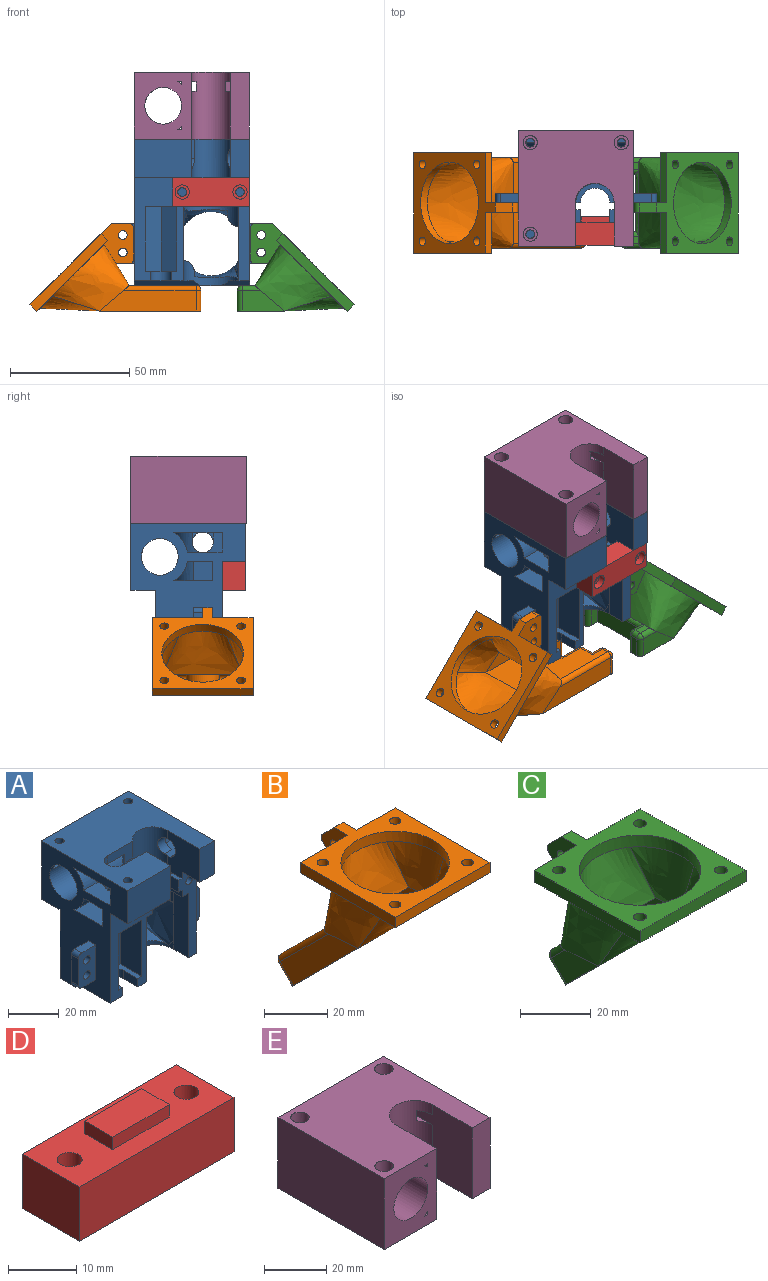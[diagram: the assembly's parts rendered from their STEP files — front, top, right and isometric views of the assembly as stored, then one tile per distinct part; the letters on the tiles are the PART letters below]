
ASSEMBLY  parts=5 mates=4
PART A: 179 faces, bbox 68x48.6x61.8 mm
  f0: plane 61.5x48.25mm, normal (1,0,0), area 1645.7mm2, adj f1,f4,f22,f24,f35,f36,f37,f43
  f1: plane 48.4x8.88mm, normal (0,0,-1), area 407.8mm2, adj f0,f5,f43,f44,f86,f87,f90,f100
  f2: plane 43.38x26.08mm, normal (0,-1,0), area 533.4mm2, adj f6,f8,f9,f13,f25,f44,f45,f47
  f3: cylinder r=4.38mm len=8.75mm, axis (0,0,-1), area 55mm2, adj f8,f9,f172,f175
  f4: plane 43.38x10.08mm, normal (0,-1,0), area 239.6mm2, adj f0,f7,f12,f29,f45,f53,f120,f164
  f5: cylinder r=11.7mm len=23.4mm, axis (0,0,1), area 147.8mm2, adj f1,f6,f7,f11,f39,f41,f174,f175
  f6: plane 31.25x8.13mm, normal (1,0,0), area 253.9mm2, adj f2,f5,f38,f40,f45,f175
  f7: plane 31.25x8.13mm, normal (-1,0,0), area 253.9mm2, adj f4,f5,f40,f41,f45,f176
  f8: plane 8.13x4mm, normal (-1,0,0), area 32.5mm2, adj f2,f3,f172,f175
  f9: plane 8.13x4mm, normal (1,0,0), area 32.5mm2, adj f2,f3,f172,f175
  f10: plane 8.56x1.84mm, normal (-1,0,0), area 8mm2, adj f40,f42,f173
  f11: plane 8.56x1.84mm, normal (1,0,0), area 8mm2, adj f5,f39,f174
  f12: plane 8.13x3.25mm, normal (-1,0,0), area 25.8mm2, adj f4,f45,f59,f109,f116,f166
  f13: plane 8.13x3.25mm, normal (1,0,0), area 25.8mm2, adj f2,f31,f45,f59,f119,f162
  f14: plane 6.57x2.69mm, normal (0,0,1), area 13.5mm2, adj f146,f147,f148,f160
  f15: plane 2.46x1.42mm, normal (0,0,-1), area 1.7mm2, adj f142,f144,f160
  f16: plane 2.46x1.42mm, normal (0,0,-1), area 1.7mm2, adj f143,f145,f160
  f17: plane 3.62x3.46mm, normal (0,1,0), area 12.6mm2, adj f141,f144,f145,f160
  f18: plane 6.57x2.69mm, normal (0,0,1), area 13.5mm2, adj f155,f156,f157,f160
  f19: plane 2.46x1.42mm, normal (0,0,-1), area 1.7mm2, adj f151,f153,f160
  f20: plane 2.46x1.42mm, normal (0,0,-1), area 1.7mm2, adj f152,f154,f160
  f21: plane 3.62x3.46mm, normal (0,1,0), area 12.6mm2, adj f150,f153,f154,f160
  f22: plane 48.4x48.25mm, normal (0,0,1), area 1761.2mm2, adj f0,f25,f26,f28,f29,f44,f46,f51
  f23: plane 8.13x6.5mm, normal (-1,0,0), area 33.5mm2, adj f24,f48,f127,f129,f130
  f24: plane 48.4x26.26mm, normal (0,0,-1), area 481.3mm2, adj f0,f23,f26,f28,f29,f44,f54,f56
  f25: plane 19.25x18.13mm, normal (1,0,0), area 267.5mm2, adj f2,f22,f28,f46,f47,f48,f111,f119
  f26: cylinder r=4.38mm len=8.75mm, axis (0,0,-1), area 55mm2, adj f22,f24,f128,f129
  f27: cylinder r=4.38mm len=5.17mm, axis (-1,0,0), area 22.2mm2, adj f28,f48,f58,f128
  f28: cylinder r=8.12mm len=19.25mm, axis (0,0,-1), area 408.2mm2, adj f22,f24,f25,f27,f29,f48,f55,f62
  f29: plane 19.25x18.13mm, normal (-1,0,0), area 288.1mm2, adj f4,f22,f24,f28,f32,f52,f53,f55
  f30: plane 8.13x3.34mm, normal (0,1,0), area 27.2mm2, adj f34,f36,f107,f124
  f31: plane 5.73x5.13mm, normal (0,0,1), area 24.6mm2, adj f13,f65,f113,f118,f119,f123
  f32: plane 5.73x5.13mm, normal (0,0,-1), area 24.6mm2, adj f29,f64,f108,f114,f116,f121
  f33: cylinder r=12.12mm len=22.89mm, axis (0,0,1), area 89.5mm2, adj f34,f35,f36,f57,f105,f106
  f34: plane 21.95x10.6mm, normal (0,0,-1), area 123mm2, adj f30,f33,f44,f49,f57,f106,f107,f124
  f35: plane 5.95x2.47mm, normal (0,0,-1), area 13.1mm2, adj f0,f33,f57,f105
  f36: plane 48.4x16.26mm, normal (0,0,1), area 328.5mm2, adj f0,f30,f33,f44,f49,f57,f105,f106
  f37: plane 5.93x5.13mm, normal (0,0,-1), area 25.2mm2, adj f0,f91,f94,f96,f97,f102
  f38: bspline ~31.25x19.88mm, area 392.3mm2, adj f6,f40,f42,f43,f85,f174
  f39: bspline ~23.4x19.88mm, area 177.2mm2, adj f5,f11,f41,f43,f174
  f40: cylinder r=11.7mm len=23.4mm, axis (0,0,1), area 123.4mm2, adj f6,f7,f10,f38,f42,f45,f173
  f41: bspline ~31.25x19.88mm, area 392.3mm2, adj f5,f7,f39,f43,f84,f173
  f42: bspline ~23.4x19.88mm, area 177.2mm2, adj f10,f38,f40,f43,f173
  f43: plane 48.4x33.25mm, normal (0,1,0), area 1029mm2, adj f0,f1,f38,f39,f41,f42,f44,f50
  f44: plane 61.5x48.25mm, normal (-1,0,0), area 1646.4mm2, adj f1,f2,f22,f24,f34,f36,f43,f46
  f45: plane 23.4x19.83mm, normal (0,0,-1), area 169.4mm2, adj f2,f4,f6,f7,f12,f13,f40,f59
  f46: plane 24.08x16.13mm, normal (0,-1,0), area 388.2mm2, adj f22,f25,f44,f47
  f47: plane 24.08x10mm, normal (0,0,-1), area 240.8mm2, adj f2,f25,f44,f46
  f48: plane 24.24x22.6mm, normal (0,0,1), area 300.1mm2, adj f23,f25,f27,f28,f44,f54,f58,f124
  f49: plane 9.74x8.13mm, normal (0,1,0), area 79.2mm2, adj f34,f36,f44,f124
  f50: plane 48.4x10.25mm, normal (0,0,-1), area 496.1mm2, adj f0,f43,f44,f51
  f51: plane 48.4x28.25mm, normal (0,1,0), area 1367.3mm2, adj f0,f22,f44,f50
  f52: plane 16.13x8.08mm, normal (0,-1,0), area 130.2mm2, adj f0,f22,f29,f53
  f53: plane 10x8.08mm, normal (0,0,-1), area 80.7mm2, adj f0,f4,f29,f52
  f54: cylinder r=11.7mm len=48.4mm, axis (-1,0,0), area 332.2mm2, adj f0,f24,f44,f48,f55,f58
  f55: plane 20.6x8.24mm, normal (0,0,1), area 100.9mm2, adj f0,f28,f29,f54,f56,f58,f63,f125
  f56: plane 8.13x4.08mm, normal (0,1,0), area 33.1mm2, adj f0,f24,f55,f63
  f57: cylinder r=11.7mm len=48.4mm, axis (-1,0,0), area 332.2mm2, adj f0,f33,f34,f35,f36,f44
  f58: cylinder r=12.12mm len=24.03mm, axis (0,0,1), area 95.3mm2, adj f24,f27,f48,f54,f55,f126,f128
  f59: cylinder r=8.12mm len=16.25mm, axis (0,0,-1), area 83mm2, adj f12,f13,f45,f60,f64,f65
  f60: plane 16.25x8.13mm, normal (0,0,-1), area 44.8mm2, adj f59,f61,f64,f65
  f61: cylinder r=6.12mm len=12.25mm, axis (0,0,-1), area 110.6mm2, adj f60,f62,f64,f65
  f62: plane 16.25x8.13mm, normal (0,0,1), area 44.8mm2, adj f28,f61,f64,f65
  f63: plane 12.5x8.13mm, normal (1,0,0), area 85.4mm2, adj f24,f55,f56,f125
  f64: plane 9.46x6mm, normal (0,-1,0), area 51.1mm2, adj f28,f32,f59,f60,f61,f62,f108,f109
  f65: plane 9.46x6mm, normal (0,-1,0), area 51.1mm2, adj f28,f31,f59,f60,f61,f62,f111,f112
  f66: plane 7.65x4mm, normal (0,0,-1), area 30.6mm2, adj f0,f67,f69,f79
  f67: plane 16.95x9.65mm, normal (0,1,0), area 140.9mm2, adj f0,f66,f68,f70,f78,f79,f82,f83
  f68: plane 7.65x4mm, normal (0,0,1), area 30.6mm2, adj f0,f67,f69,f78
  f69: plane 16.95x9.65mm, normal (0,-1,0), area 140.9mm2, adj f0,f66,f68,f70,f78,f79,f82,f83
  f70: plane 12.95x4mm, normal (1,0,0), area 51.8mm2, adj f67,f69,f78,f79
  f71: plane 7.65x4mm, normal (0,0,-1), area 30.6mm2, adj f44,f72,f74,f76
  f72: plane 16.95x9.65mm, normal (0,-1,0), area 140.9mm2, adj f44,f71,f73,f75,f76,f77,f80,f81
  f73: plane 7.65x4mm, normal (0,0,1), area 30.6mm2, adj f44,f72,f74,f77
  f74: plane 16.95x9.65mm, normal (0,1,0), area 140.9mm2, adj f44,f71,f73,f75,f76,f77,f80,f81
  f75: plane 12.95x4mm, normal (-1,0,0), area 51.8mm2, adj f72,f74,f76,f77
  f76: cylinder r=2mm len=4mm, axis (0,1,0), area 12.6mm2, adj f71,f72,f74,f75
  f77: cylinder r=2mm len=4mm, axis (0,-1,0), area 12.6mm2, adj f72,f73,f74,f75
  f78: cylinder r=2mm len=4mm, axis (0,1,0), area 12.6mm2, adj f67,f68,f69,f70
  f79: cylinder r=2mm len=4mm, axis (0,-1,0), area 12.6mm2, adj f66,f67,f69,f70
  f80: cylinder r=1.82mm len=4mm, axis (0,1,0), area 45.9mm2, adj f72,f74
  f81: cylinder r=1.82mm len=4mm, axis (0,1,0), area 45.9mm2, adj f72,f74
  f82: cylinder r=1.82mm len=4mm, axis (0,1,0), area 45.9mm2, adj f67,f69
  f83: cylinder r=1.82mm len=4mm, axis (0,1,0), area 45.9mm2, adj f67,f69
  f84: plane 1.91x0.01mm, normal (0,0,-1), area 0mm2, adj f41,f173
  f85: plane 1.91x0.01mm, normal (0,0,1), area 0mm2, adj f38,f174
  f86: plane 7.36x5.13mm, normal (-1,0,0), area 29.4mm2, adj f1,f89,f90,f98,f100,f104
  f87: plane 7.36x5.13mm, normal (1,0,0), area 29.4mm2, adj f1,f88,f90,f99,f100,f104
  f88: plane 5.13x3mm, normal (0.5,0,-0.87), area 17.8mm2, adj f87,f89,f90,f104
  f89: plane 5.13x3mm, normal (-0.5,0,-0.87), area 17.8mm2, adj f86,f88,f90,f104
  f90: plane 9.09x6mm, normal (0,1,0), area 49.3mm2, adj f1,f86,f87,f88,f89
  f91: plane 5.13x3mm, normal (0.87,0,-0.5), area 17.8mm2, adj f37,f93,f94,f102
  f92: plane 5.93x5.13mm, normal (0,0,1), area 25.2mm2, adj f0,f93,f94,f95,f97,f102
  f93: plane 5.13x3mm, normal (0.87,0,0.5), area 17.8mm2, adj f91,f92,f94,f102
  f94: plane 7.66x6mm, normal (0,1,0), area 40.8mm2, adj f0,f37,f91,f92,f93
  f95: plane 3x2.13mm, normal (-0.87,0,0.5), area 7.4mm2, adj f92,f96,f97,f102
  f96: plane 3x2.13mm, normal (-0.87,0,-0.5), area 7.4mm2, adj f37,f95,f97,f102
  f97: plane 6x2.47mm, normal (0,-1,0), area 9.6mm2, adj f0,f37,f92,f95,f96
  f98: plane 3x2.13mm, normal (-0.5,0,0.87), area 7.4mm2, adj f86,f99,f100,f104
  f99: plane 3x2.13mm, normal (0.5,0,0.87), area 7.4mm2, adj f87,f98,f100,f104
  f100: plane 6x3.89mm, normal (0,-1,0), area 18.2mm2, adj f1,f86,f87,f98,f99
  f101: cylinder r=1.82mm len=3.65mm, axis (0,1,0), area 34.4mm2, adj f43,f102
  f102: plane 6.93x6mm, normal (0,-1,0), area 20.7mm2, adj f37,f91,f92,f93,f95,f96,f101
  f103: cylinder r=1.82mm len=3.65mm, axis (0,1,0), area 34.4mm2, adj f43,f104
  f104: plane 6.93x6mm, normal (0,-1,0), area 20.7mm2, adj f86,f87,f88,f89,f98,f99,f103
  f105: plane 8.13x4.75mm, normal (0,1,0), area 38.6mm2, adj f0,f33,f35,f36
  f106: plane 8.13x4.75mm, normal (0,1,0), area 38.6mm2, adj f33,f34,f36,f107
  f107: plane 8.13x8.13mm, normal (-1,0,0), area 66mm2, adj f30,f34,f36,f106
  f108: plane 5.13x3mm, normal (-0.87,0,-0.5), area 17.8mm2, adj f32,f64,f110,f121
  f109: plane 5.73x5.13mm, normal (0,0,1), area 24.6mm2, adj f12,f64,f110,f115,f116,f121
  f110: plane 5.13x3mm, normal (-0.87,0,0.5), area 17.8mm2, adj f64,f108,f109,f121
  f111: plane 5.73x5.13mm, normal (0,0,-1), area 24.6mm2, adj f25,f65,f112,f117,f119,f123
  f112: plane 5.13x3mm, normal (0.87,0,-0.5), area 17.8mm2, adj f65,f111,f113,f123
  f113: plane 5.13x3mm, normal (0.87,0,0.5), area 17.8mm2, adj f31,f65,f112,f123
  f114: plane 3x2.13mm, normal (0.87,0,-0.5), area 7.4mm2, adj f32,f115,f116,f121
  f115: plane 3x2.13mm, normal (0.87,0,0.5), area 7.4mm2, adj f109,f114,f116,f121
  f116: plane 6x4.27mm, normal (0,1,0), area 19.9mm2, adj f12,f29,f32,f109,f114,f115,f164,f165
  f117: plane 3x2.13mm, normal (-0.87,0,-0.5), area 7.4mm2, adj f111,f118,f119,f123
  f118: plane 3x2.13mm, normal (-0.87,0,0.5), area 7.4mm2, adj f31,f117,f119,f123
  f119: plane 6x4.27mm, normal (0,1,0), area 19.9mm2, adj f13,f25,f31,f111,f117,f118,f161,f162
  f120: cylinder r=1.82mm len=3.65mm, axis (0,-1,0), area 34.4mm2, adj f4,f121
  f121: plane 6.93x6mm, normal (0,1,0), area 20.7mm2, adj f32,f108,f109,f110,f114,f115,f120
  f122: cylinder r=1.82mm len=3.65mm, axis (0,-1,0), area 34.4mm2, adj f2,f123
  f123: plane 6.93x6mm, normal (0,1,0), area 20.7mm2, adj f31,f111,f112,f113,f117,f118,f122
  f124: cylinder r=4.38mm len=16.13mm, axis (0,0,-1), area 244.1mm2, adj f30,f34,f36,f48,f49,f167
  f125: cylinder r=4.38mm len=8.13mm, axis (-1,0,0), area 41.7mm2, adj f24,f29,f55,f63
  f126: cylinder r=4.38mm len=8.13mm, axis (-1,0,0), area 48.9mm2, adj f24,f28,f55,f58
  f127: cylinder r=4.38mm len=4.06mm, axis (-1,0,0), area 20.8mm2, adj f23,f25,f48,f129
  f128: plane 14.15x8.06mm, normal (0,-1,0), area 74.7mm2, adj f22,f24,f26,f27,f28,f58
  f129: plane 12.88x8.06mm, normal (0,1,0), area 67.8mm2, adj f22,f23,f24,f25,f26,f127
  f130: plane 20.08x8.13mm, normal (0,1,0), area 134.5mm2, adj f23,f24,f44,f48,f132,f133,f139
  f131: plane 8.13x3mm, normal (-0.87,0.5,0), area 28.1mm2, adj f48,f132,f135,f137,f159
  f132: plane 5x4.13mm, normal (-1,0,0), area 20.6mm2, adj f48,f130,f131,f139
  f133: plane 5x4.13mm, normal (1,0,0), area 20.6mm2, adj f48,f130,f134,f139
  f134: plane 8.13x3mm, normal (0.87,0.5,0), area 28.1mm2, adj f48,f133,f135,f138,f159
  f135: plane 8.13x3.46mm, normal (0,1,0), area 28.1mm2, adj f48,f131,f134,f159
  f136: plane 4x3.46mm, normal (0,-1,0), area 13.9mm2, adj f137,f138,f139,f159
  f137: plane 4x3mm, normal (-0.87,-0.5,0), area 13.9mm2, adj f131,f136,f139,f159
  f138: plane 4x3mm, normal (0.87,-0.5,0), area 13.9mm2, adj f134,f136,f139,f159
  f139: plane 6.93x5mm, normal (0,0,-1), area 19.1mm2, adj f130,f132,f133,f136,f137,f138
  f140: cylinder r=1.82mm len=4mm, axis (0,0,1), area 45.9mm2, adj f22,f141
  f141: plane 6.93x6mm, normal (0,0,-1), area 20.7mm2, adj f17,f140,f144,f145,f146,f147,f148
  f142: plane 3.21x2.46mm, normal (1,0,0), area 3.2mm2, adj f15,f148,f160
  f143: plane 3.21x2.46mm, normal (-1,0,0), area 3.2mm2, adj f16,f147,f160
  f144: plane 4x3mm, normal (0.87,0.5,0), area 13.7mm2, adj f15,f17,f141,f148,f160
  f145: plane 4x3mm, normal (-0.87,0.5,0), area 13.7mm2, adj f16,f17,f141,f147,f160
  f146: plane 8.13x3.46mm, normal (0,-1,0), area 28.1mm2, adj f14,f141,f147,f148
  f147: plane 8.14x3.02mm, normal (-0.87,-0.5,0), area 28mm2, adj f14,f141,f143,f145,f146,f160
  f148: plane 8.14x3.02mm, normal (0.87,-0.5,0), area 28mm2, adj f14,f141,f142,f144,f146,f160
  f149: cylinder r=1.82mm len=4mm, axis (0,0,1), area 45.9mm2, adj f22,f150
  f150: plane 6.93x6mm, normal (0,0,-1), area 20.7mm2, adj f21,f149,f153,f154,f155,f156,f157
  f151: plane 3.21x2.46mm, normal (1,0,0), area 3.2mm2, adj f19,f157,f160
  f152: plane 3.21x2.46mm, normal (-1,0,0), area 3.2mm2, adj f20,f156,f160
  f153: plane 4x3mm, normal (0.87,0.5,0), area 13.7mm2, adj f19,f21,f150,f157,f160
  f154: plane 4x3mm, normal (-0.87,0.5,0), area 13.7mm2, adj f20,f21,f150,f156,f160
  f155: plane 8.13x3.46mm, normal (0,-1,0), area 28.1mm2, adj f18,f150,f156,f157
  f156: plane 8.14x3.02mm, normal (-0.87,-0.5,0), area 28mm2, adj f18,f150,f152,f154,f155,f160
  f157: plane 8.14x3.02mm, normal (0.87,-0.5,0), area 28mm2, adj f18,f150,f151,f153,f155,f160
  f158: cylinder r=1.82mm len=4mm, axis (0,0,1), area 45.9mm2, adj f22,f159
  f159: plane 6.93x6mm, normal (0,0,-1), area 20.7mm2, adj f131,f134,f135,f136,f137,f138,f158
  f160: cylinder r=7.7mm len=48.4mm, axis (-1,0,0), area 2266.9mm2, adj f0,f14,f15,f16,f17,f18,f19,f20
  f161: plane 5.13x2mm, normal (0,0,1), area 10.3mm2, adj f2,f25,f119,f163
  f162: plane 5.13x2mm, normal (0,0,-1), area 10.3mm2, adj f2,f13,f119,f163
  f163: plane 5.75x5.13mm, normal (1,0,0), area 29.5mm2, adj f2,f119,f161,f162
  f164: plane 5.13x2mm, normal (0,0,1), area 10.3mm2, adj f4,f29,f116,f165
  f165: plane 5.75x5.13mm, normal (-1,0,0), area 29.5mm2, adj f4,f116,f164,f166
  f166: plane 5.13x2mm, normal (0,0,-1), area 10.3mm2, adj f4,f12,f116,f165
  f167: plane 15.86x13.4mm, normal (0,0,-1), area 126.5mm2, adj f2,f124,f168,f169,f170,f171
  f168: plane 27.25x11.99mm, normal (1,0,0), area 326.8mm2, adj f2,f167,f169,f172
  f169: plane 27.25x6.7mm, normal (0.5,-0.87,0), area 210.8mm2, adj f167,f168,f170,f172
  f170: plane 27.25x6.7mm, normal (-0.5,-0.87,0), area 210.8mm2, adj f167,f169,f171,f172
  f171: plane 27.25x11.99mm, normal (-1,0,0), area 326.8mm2, adj f2,f167,f170,f172
  f172: plane 15.86x13.4mm, normal (0,0,1), area 85.5mm2, adj f2,f3,f8,f9,f168,f169,f170,f171
  f173: cylinder r=5mm len=19.88mm, axis (0,1,0), area 96.3mm2, adj f10,f40,f41,f42,f43,f84
  f174: cylinder r=5mm len=19.88mm, axis (0,1,0), area 96.3mm2, adj f5,f11,f38,f39,f43,f85
  f175: plane 24.72x17.13mm, normal (0,0,-1), area 261.5mm2, adj f2,f3,f5,f6,f8,f9,f44,f177
  f176: plane 17.13x8.72mm, normal (0,0,-1), area 88.7mm2, adj f0,f4,f5,f7,f178
  f177: plane 28.52x2.3mm, normal (0,-0.71,-0.71), area 74.2mm2, adj f1,f5,f44,f175
  f178: plane 12.52x2.3mm, normal (0,-0.71,-0.71), area 28.9mm2, adj f0,f1,f5,f176
PART B: 86 faces, bbox 44.4x57.7x54.7 mm
  f0: plane 6.08x6.08mm, normal (0,0.71,-0.71), area 43mm2, adj f8,f15,f80,f81
  f1: plane 7x4.67mm, normal (0,-0.71,0.71), area 46.2mm2, adj f3,f8,f29,f64
  f2: cylinder r=2mm len=10mm, axis (1,0,0), area 31.4mm2, adj f5,f8,f24,f64
  f3: cylinder r=2mm len=10mm, axis (1,0,0), area 31.4mm2, adj f1,f4,f24,f25,f64
  f4: plane 34x15.87mm, normal (0,-0.71,-0.71), area 588.3mm2, adj f3,f22,f23,f24,f38,f64,f65,f66
  f5: plane 34x19.22mm, normal (0,0.71,0.71), area 791.2mm2, adj f2,f21,f23,f24,f40,f64,f65,f66
  f6: plane 21.13x4mm, normal (0,1,0), area 84.5mm2, adj f41,f44,f51,f60
  f7: plane 7x4.67mm, normal (0,-0.71,0.71), area 46.2mm2, adj f8,f22,f34,f66
  f8: plane 38x30.07mm, normal (0,-0.71,-0.71), area 1221.5mm2, adj f0,f1,f2,f7,f9,f11,f12,f13
  f9: plane 6.08x6.08mm, normal (0,0.71,-0.71), area 43mm2, adj f8,f13,f76,f77
  f10: plane 34x19.87mm, normal (0,0.71,0.71), area 584.6mm2, adj f18,f20,f35,f69,f72,f74,f77,f78
  f11: plane 6.08x6.08mm, normal (0,0.71,-0.71), area 25.8mm2, adj f8,f19,f68,f69
  f12: plane 36.3x30.22mm, normal (1,0,0), area 305.2mm2, adj f8,f19,f20,f35
  f13: plane 8.91x8.91mm, normal (-1,0,0), area 34.4mm2, adj f8,f9,f68,f74
  f14: plane 6.08x6.08mm, normal (0,0.71,-0.71), area 25.8mm2, adj f8,f17,f72,f73
  f15: plane 8.91x8.91mm, normal (1,0,0), area 34.4mm2, adj f0,f8,f73,f78
  f16: plane 36.3x30.22mm, normal (-1,0,0), area 305.2mm2, adj f8,f17,f18,f35
  f17: cylinder r=2mm len=7.5mm, axis (0,0.71,0.71), area 27mm2, adj f8,f14,f16,f70
  f18: cylinder r=2mm len=22.94mm, axis (0,-0.71,0.71), area 92mm2, adj f10,f16,f35,f70
  f19: cylinder r=2mm len=7.5mm, axis (0,-0.71,-0.71), area 27mm2, adj f8,f11,f12,f67
  f20: cylinder r=2mm len=22.94mm, axis (0,0.71,-0.71), area 92mm2, adj f10,f12,f35,f67
  f21: cylinder r=2mm len=10mm, axis (1,0,0), area 31.4mm2, adj f5,f8,f23,f66
  f22: cylinder r=2mm len=10mm, axis (1,0,0), area 31.4mm2, adj f4,f7,f23,f30,f66
  f23: plane 30.84x28.41mm, normal (1,0,0), area 243.6mm2, adj f4,f5,f8,f21,f22,f30,f31,f32
  f24: plane 30.84x28.41mm, normal (-1,0,0), area 243.6mm2, adj f2,f3,f4,f5,f8,f25,f26,f27
  f25: plane 3x1.41mm, normal (0,0.71,-0.71), area 6mm2, adj f3,f24,f28,f29
  f26: plane 4.67x4.67mm, normal (0,-0.71,0.71), area 19.8mm2, adj f8,f24,f27,f29
  f27: cylinder r=2mm len=3mm, axis (-1,0,0), area 9.4mm2, adj f24,f26,f28,f29
  f28: plane 3x2.83mm, normal (0,-0.71,-0.71), area 12mm2, adj f24,f25,f27,f29
  f29: plane 10.32x9.5mm, normal (1,0,0), area 50.7mm2, adj f1,f8,f25,f26,f27,f28
  f30: plane 3x1.41mm, normal (0,0.71,-0.71), area 6mm2, adj f22,f23,f33,f34
  f31: plane 4.67x4.67mm, normal (0,-0.71,0.71), area 19.8mm2, adj f8,f23,f32,f34
  f32: cylinder r=2mm len=3mm, axis (-1,0,0), area 9.4mm2, adj f23,f31,f33,f34
  f33: plane 3x2.83mm, normal (0,-0.71,-0.71), area 12mm2, adj f23,f30,f32,f34
  f34: plane 10.32x9.5mm, normal (-1,0,0), area 50.7mm2, adj f7,f8,f30,f31,f32,f33
  f35: bspline ~38.21x31.04mm, area 1454.7mm2, adj f10,f12,f16,f18,f20,f36,f41,f52
  f36: bspline ~38x18.47mm, area 813.9mm2, adj f8,f35,f41
  f37: bspline ~19.51x19.15mm, area 298.3mm2, adj f23,f38,f40,f48
  f38: bspline ~34x19.51mm, area 552.1mm2, adj f4,f37,f39,f48
  f39: bspline ~19.51x19.15mm, area 298.3mm2, adj f24,f38,f40,f48
  f40: bspline ~34x18.71mm, area 854.1mm2, adj f5,f37,f39,f48
  f41: plane 44.37x44.37mm, normal (0,0,-1), area 585.6mm2, adj f6,f35,f36,f42,f43,f44,f45,f46
  f42: plane 42.25x4mm, normal (1,0,0), area 169mm2, adj f41,f43,f50,f51
  f43: plane 17.13x4mm, normal (0,1,0), area 68.5mm2, adj f41,f42,f51,f59
  f44: plane 42.25x4mm, normal (-1,0,0), area 169mm2, adj f6,f41,f50,f51
  f45: cylinder r=1.82mm len=4mm, axis (0,0,-1), area 45.9mm2, adj f41,f51
  f46: cylinder r=1.82mm len=4mm, axis (0,0,-1), area 45.9mm2, adj f41,f51
  f47: cylinder r=1.82mm len=4mm, axis (0,0,-1), area 45.9mm2, adj f41,f51
  f48: cylinder r=17.12mm len=34.25mm, axis (0,0,-1), area 430.4mm2, adj f37,f38,f39,f40,f51
  f49: cylinder r=1.82mm len=4mm, axis (0,0,-1), area 45.9mm2, adj f41,f51
  f50: plane 42.25x4mm, normal (0,-1,0), area 169mm2, adj f41,f42,f44,f51
  f51: plane 48.25x42.25mm, normal (0,0,1), area 845.9mm2, adj f6,f42,f43,f44,f45,f46,f47,f48
  f52: plane 4.04x3.81mm, normal (0,-0.71,-0.71), area 21.2mm2, adj f35,f53,f59,f60
  f53: cylinder r=2mm len=4mm, axis (-1,0,0), area 12.6mm2, adj f52,f54,f59,f60
  f54: plane 9.16x9.16mm, normal (0,0.71,-0.71), area 51.8mm2, adj f53,f55,f59,f60
  f55: cylinder r=2mm len=4mm, axis (-1,0,0), area 12.6mm2, adj f54,f57,f59,f60
  f56: cylinder r=1.82mm len=4mm, axis (-1,0,0), area 45.9mm2, adj f59,f60
  f57: plane 5.23x5.23mm, normal (0,0.71,0.71), area 29.6mm2, adj f51,f55,f59,f60
  f58: cylinder r=1.82mm len=4mm, axis (-1,0,0), area 45.9mm2, adj f59,f60
  f59: plane 18.52x17.06mm, normal (1,0,0), area 161.3mm2, adj f35,f41,f43,f51,f52,f53,f54,f55
  f60: plane 17.8x16.3mm, normal (-1,0,0), area 159.6mm2, adj f6,f35,f41,f51,f52,f53,f54,f55
  f61: plane 12.45x12.45mm, normal (1,0,0), area 77.4mm2, adj f8,f62,f81,f85
  f62: cylinder r=5mm len=10mm, axis (0,-0.71,-0.71), area 135.1mm2, adj f8,f61,f63,f84
  f63: plane 12.45x12.45mm, normal (-1,0,0), area 77.4mm2, adj f8,f62,f76,f82
  f64: plane 12.45x10.2mm, normal (1,0,0), area 65.4mm2, adj f1,f2,f3,f4,f5,f8,f65
  f65: cylinder r=7mm len=14mm, axis (0,-0.71,-0.71), area 145.1mm2, adj f4,f5,f64,f66
  f66: plane 12.45x10.2mm, normal (-1,0,0), area 65.4mm2, adj f4,f5,f7,f8,f21,f22,f65
  f67: sphere r=2mm, area 4.7mm2, adj f19,f20,f69
  f68: cylinder r=2mm len=7.5mm, axis (0,0.71,0.71), area 27mm2, adj f8,f11,f13,f71
  f69: cylinder r=2mm len=3mm, axis (1,0,0), area 9.4mm2, adj f10,f11,f67,f71
  f70: sphere r=2mm, area 4.7mm2, adj f17,f18,f72
  f71: sphere r=2mm, area 4.7mm2, adj f68,f69,f74
  f72: cylinder r=2mm len=3mm, axis (1,0,0), area 9.4mm2, adj f10,f14,f70,f75
  f73: cylinder r=2mm len=7.5mm, axis (0,-0.71,-0.71), area 27mm2, adj f8,f14,f15,f75
  f74: cylinder r=2mm len=5.66mm, axis (0,-0.71,0.71), area 15.7mm2, adj f10,f13,f71,f77
  f75: sphere r=2mm, area 4.7mm2, adj f72,f73,f78
  f76: cylinder r=2mm len=7.5mm, axis (0,-0.71,-0.71), area 27mm2, adj f8,f9,f63,f79
  f77: cylinder r=2mm len=7mm, axis (-1,0,0), area 18.8mm2, adj f9,f10,f74,f79
  f78: cylinder r=2mm len=5.66mm, axis (0,0.71,-0.71), area 15.7mm2, adj f10,f15,f75,f80
  f79: sphere r=2mm, area 4.7mm2, adj f76,f77,f82
  f80: cylinder r=2mm len=7mm, axis (-1,0,0), area 18.8mm2, adj f0,f10,f78,f83
  f81: cylinder r=2mm len=7.5mm, axis (0,0.71,0.71), area 27mm2, adj f0,f8,f61,f83
  f82: cylinder r=2mm len=7.78mm, axis (0,-0.71,0.71), area 28.3mm2, adj f10,f63,f79,f84
  f83: sphere r=2mm, area 5.5mm2, adj f80,f81,f85
  f84: torus R=7mm, axis (0,0.71,0.71), area 56.5mm2, adj f10,f62,f82,f85
  f85: cylinder r=2mm len=7.78mm, axis (0,0.71,-0.71), area 28.3mm2, adj f10,f61,f83,f84
PART C: 64 faces, bbox 44.4x56.2x38.6 mm
  f0: plane 4.3x4.3mm, normal (0,0.71,0.71), area 16.1mm2, adj f1,f15,f17,f61
  f1: bspline ~38.21x31.04mm, area 1454.4mm2, adj f0,f2,f7,f9,f13,f15,f21,f33
  f2: plane 44.37x44.37mm, normal (0,0,-1), area 585.6mm2, adj f1,f3,f33,f38,f39,f40,f41,f42
  f3: plane 17.13x4mm, normal (0,1,0), area 68.5mm2, adj f2,f40,f47,f55
  f4: plane 28x6.08mm, normal (0,-0.71,0.71), area 240.8mm2, adj f5,f24,f29,f32
  f5: plane 38x13.98mm, normal (0,-0.71,-0.71), area 466mm2, adj f4,f6,f8,f9,f10,f11,f12,f13
  f6: plane 24.01x6.16mm, normal (0,0.71,-0.71), area 209mm2, adj f5,f10,f12,f17,f19,f63
  f7: plane 4.3x4.3mm, normal (0,0.71,0.71), area 16.1mm2, adj f1,f19,f21,f58
  f8: plane 6.08x6.08mm, normal (0,0.71,-0.71), area 25.8mm2, adj f5,f18,f20,f58
  f9: plane 20.22x14.13mm, normal (1,0,0), area 109.5mm2, adj f1,f5,f20,f21
  f10: plane 8.91x8.91mm, normal (-1,0,0), area 34.4mm2, adj f5,f6,f18,f19
  f11: plane 6.08x6.08mm, normal (0,0.71,-0.71), area 25.8mm2, adj f5,f14,f16,f61
  f12: plane 8.91x8.91mm, normal (1,0,0), area 34.4mm2, adj f5,f6,f16,f17
  f13: plane 20.22x14.13mm, normal (-1,0,0), area 109.5mm2, adj f1,f5,f14,f15
  f14: cylinder r=2mm len=7.5mm, axis (0,0.71,0.71), area 27mm2, adj f5,f11,f13,f60
  f15: cylinder r=2mm len=6.86mm, axis (0,-0.71,0.71), area 20.5mm2, adj f0,f1,f13,f60
  f16: cylinder r=2mm len=7.5mm, axis (0,-0.71,-0.71), area 27mm2, adj f5,f11,f12,f62
  f17: cylinder r=2mm len=5.2mm, axis (0,0.71,-0.71), area 14.4mm2, adj f0,f6,f12,f62,f63
  f18: cylinder r=2mm len=7.5mm, axis (0,0.71,0.71), area 27mm2, adj f5,f8,f10,f57
  f19: cylinder r=2mm len=5.2mm, axis (0,-0.71,0.71), area 14.4mm2, adj f6,f7,f10,f57,f63
  f20: cylinder r=2mm len=7.5mm, axis (0,-0.71,-0.71), area 27mm2, adj f5,f8,f9,f59
  f21: cylinder r=2mm len=6.86mm, axis (0,0.71,-0.71), area 20.5mm2, adj f1,f7,f9,f59
  f22: plane 34x3.13mm, normal (0,0.71,0.71), area 150.7mm2, adj f23,f25,f26,f37
  f23: cylinder r=2mm len=34mm, axis (1,0,0), area 106.8mm2, adj f5,f22,f25,f26
  f24: plane 34x4.03mm, normal (0,-0.71,-0.71), area 81.7mm2, adj f4,f25,f26,f28,f29,f31,f32,f35
  f25: plane 14.75x12.33mm, normal (1,0,0), area 94.3mm2, adj f5,f22,f23,f24,f27,f28,f34
  f26: plane 14.75x12.33mm, normal (-1,0,0), area 94.3mm2, adj f5,f22,f23,f24,f30,f31,f36
  f27: plane 4.67x4.67mm, normal (0,-0.71,0.71), area 19.8mm2, adj f5,f25,f28,f29
  f28: cylinder r=2mm len=3mm, axis (1,0,0), area 9.4mm2, adj f24,f25,f27,f29
  f29: plane 10.32x9.5mm, normal (-1,0,0), area 50.7mm2, adj f4,f5,f24,f27,f28
  f30: plane 4.67x4.67mm, normal (0,-0.71,0.71), area 19.8mm2, adj f5,f26,f31,f32
  f31: cylinder r=2mm len=3mm, axis (1,0,0), area 9.4mm2, adj f24,f26,f30,f32
  f32: plane 10.32x9.5mm, normal (1,0,0), area 50.7mm2, adj f4,f5,f24,f30,f31
  f33: bspline ~38x18.47mm, area 813.9mm2, adj f1,f2,f5
  f34: bspline ~19.51x19.15mm, area 298.3mm2, adj f25,f35,f37,f44
  f35: bspline ~34x19.51mm, area 552.1mm2, adj f24,f34,f36,f44
  f36: bspline ~19.51x19.15mm, area 298.3mm2, adj f26,f35,f37,f44
  f37: bspline ~34x18.71mm, area 854.1mm2, adj f22,f34,f36,f44
  f38: plane 42.25x4mm, normal (1,0,0), area 169mm2, adj f2,f39,f46,f47
  f39: plane 21.13x4mm, normal (0,1,0), area 84.5mm2, adj f2,f38,f47,f56
  f40: plane 42.25x4mm, normal (-1,0,0), area 169mm2, adj f2,f3,f46,f47
  f41: cylinder r=1.82mm len=4mm, axis (0,0,-1), area 45.9mm2, adj f2,f47
  f42: cylinder r=1.82mm len=4mm, axis (0,0,-1), area 45.9mm2, adj f2,f47
  f43: cylinder r=1.82mm len=4mm, axis (0,0,-1), area 45.9mm2, adj f2,f47
  f44: cylinder r=17.12mm len=34.25mm, axis (0,0,-1), area 430.4mm2, adj f34,f35,f36,f37,f47
  f45: cylinder r=1.82mm len=4mm, axis (0,0,-1), area 45.9mm2, adj f2,f47
  f46: plane 42.25x4mm, normal (0,-1,0), area 169mm2, adj f2,f38,f40,f47
  f47: plane 48.25x42.25mm, normal (0,0,1), area 845.9mm2, adj f3,f38,f39,f40,f41,f42,f43,f44
  f48: plane 4.04x3.81mm, normal (0,-0.71,-0.71), area 21.2mm2, adj f1,f49,f55,f56
  f49: cylinder r=2mm len=4mm, axis (1,0,0), area 12.6mm2, adj f48,f50,f55,f56
  f50: plane 9.16x9.16mm, normal (0,0.71,-0.71), area 51.8mm2, adj f49,f51,f55,f56
  f51: cylinder r=2mm len=4mm, axis (1,0,0), area 12.6mm2, adj f50,f53,f55,f56
  f52: cylinder r=1.82mm len=4mm, axis (1,0,0), area 45.9mm2, adj f55,f56
  f53: plane 5.23x5.23mm, normal (0,0.71,0.71), area 29.6mm2, adj f47,f51,f55,f56
  f54: cylinder r=1.82mm len=4mm, axis (1,0,0), area 45.9mm2, adj f55,f56
  f55: plane 18.52x17.06mm, normal (-1,0,0), area 161.3mm2, adj f1,f2,f3,f47,f48,f49,f50,f51
  f56: plane 17.8x16.3mm, normal (1,0,0), area 159.6mm2, adj f1,f2,f39,f47,f48,f49,f50,f51
  f57: sphere r=2mm, area 4.7mm2, adj f18,f19,f58
  f58: cylinder r=2mm len=3mm, axis (1,0,0), area 9.4mm2, adj f7,f8,f57,f59
  f59: sphere r=2mm, area 4.7mm2, adj f20,f21,f58
  f60: sphere r=2mm, area 4.7mm2, adj f14,f15,f61
  f61: cylinder r=2mm len=3mm, axis (1,0,0), area 9.4mm2, adj f0,f11,f60,f62
  f62: sphere r=2mm, area 4.7mm2, adj f16,f17,f61
  f63: bspline ~30.77x2.3mm, area 64.6mm2, adj f1,f6,f17,f19
PART D: 17 faces, bbox 32.2x11.9x12 mm
  f0: cylinder r=1.82mm len=6.75mm, axis (0,0,1), area 77.4mm2, adj f7,f13
  f1: cylinder r=1.82mm len=6.75mm, axis (0,0,1), area 77.4mm2, adj f7,f15
  f2: plane 32.15x9.75mm, normal (0,-1,0), area 313.5mm2, adj f3,f5,f6,f7
  f3: plane 11.88x9.75mm, normal (1,0,0), area 115.8mm2, adj f2,f4,f6,f7
  f4: plane 32.15x9.75mm, normal (0,1,0), area 313.5mm2, adj f3,f5,f6,f7
  f5: plane 11.88x9.75mm, normal (-1,0,0), area 115.8mm2, adj f2,f4,f6,f7
  f6: plane 32.15x11.88mm, normal (0,0,-1), area 326.2mm2, adj f2,f3,f4,f5,f14,f16
  f7: plane 32.15x11.88mm, normal (0,0,1), area 293.3mm2, adj f0,f1,f2,f3,f4,f5,f8,f9
  f8: plane 11.75x2.25mm, normal (0,-1,0), area 26.4mm2, adj f7,f9,f11,f12
  f9: plane 5.75x2.25mm, normal (1,0,0), area 12.9mm2, adj f7,f8,f10,f12
  f10: plane 11.75x2.25mm, normal (0,1,0), area 26.4mm2, adj f7,f9,f11,f12
  f11: plane 5.75x2.25mm, normal (-1,0,0), area 12.9mm2, adj f7,f8,f10,f12
  f12: plane 11.75x5.75mm, normal (0,0,1), area 67.6mm2, adj f8,f9,f10,f11
  f13: plane 5.95x5.95mm, normal (0,0,-1), area 17.3mm2, adj f0,f14
  f14: cylinder r=2.98mm len=5.95mm, axis (0,0,-1), area 56.1mm2, adj f6,f13
  f15: plane 5.95x5.95mm, normal (0,0,-1), area 17.3mm2, adj f1,f16
  f16: cylinder r=2.98mm len=5.95mm, axis (0,0,-1), area 56.1mm2, adj f6,f15
PART E: 44 faces, bbox 48.3x48.4x28 mm
  f0: plane 28x27.2mm, normal (1,0,0), area 545.6mm2, adj f1,f2,f6,f9,f16,f23,f43
  f1: plane 48.4x26.05mm, normal (0,0,-1), area 526.1mm2, adj f0,f2,f3,f9,f10,f15,f21,f22
  f2: cylinder r=12.12mm len=12.13mm, axis (0,0,1), area 90.5mm2, adj f0,f1,f3,f14,f15,f24,f38,f43
  f3: plane 12.2x8mm, normal (0,1,0), area 77.6mm2, adj f1,f2,f10,f14,f22,f39,f40
  f4: cylinder r=2.98mm len=24.25mm, axis (0,0,1), area 346.2mm2, adj f6,f34,f37
  f5: cylinder r=2.98mm len=24.25mm, axis (0,0,1), area 346.2mm2, adj f6,f36,f37
  f6: plane 48.4x48.25mm, normal (0,0,1), area 1852.4mm2, adj f0,f4,f5,f9,f17,f19,f20,f21
  f7: cylinder r=1.82mm len=3.75mm, axis (0,0,1), area 43mm2, adj f16,f33
  f8: cylinder r=1.82mm len=3.75mm, axis (0,0,1), area 43mm2, adj f16,f34
  f9: plane 28x23.93mm, normal (0,-1,0), area 481.6mm2, adj f0,f1,f6,f11,f15,f16,f18,f19
  f10: plane 8.08x8mm, normal (-1,0,0), area 64.6mm2, adj f1,f3,f14,f29
  f11: plane 48.4x26.05mm, normal (0,0,1), area 494.8mm2, adj f9,f13,f18,f21,f25,f26,f27,f30
  f12: plane 21.45x20.6mm, normal (0,0,-1), area 321.2mm2, adj f13,f18,f21,f25,f26,f30,f31
  f13: plane 8.08x8mm, normal (-1,0,0), area 64.6mm2, adj f11,f12,f25,f30
  f14: plane 21.45x20.6mm, normal (0,0,1), area 321.2mm2, adj f2,f3,f10,f15,f21,f28,f29
  f15: cylinder r=11.7mm len=48.4mm, axis (0,1,0), area 288.5mm2, adj f1,f2,f9,f14,f21,f24
  f16: plane 48.4x48.25mm, normal (0,0,-1), area 1904.5mm2, adj f0,f7,f8,f9,f17,f19,f20,f21
  f17: plane 48.4x28mm, normal (1,0,0), area 1355.2mm2, adj f6,f16,f20,f21
  f18: cylinder r=11.7mm len=48.4mm, axis (0,1,0), area 288.5mm2, adj f9,f11,f12,f21,f26,f27
  f19: plane 48.4x28mm, normal (-1,0,0), area 1355.2mm2, adj f6,f9,f16,f21
  f20: plane 28x8.08mm, normal (0,-1,0), area 226.1mm2, adj f6,f16,f17,f22
  f21: plane 48.25x28mm, normal (0,1,0), area 901.2mm2, adj f1,f6,f11,f12,f14,f15,f16,f17
  f22: plane 30.33x28mm, normal (-1,0,0), area 558.1mm2, adj f1,f3,f6,f16,f20,f23,f39
  f23: cylinder r=8.12mm len=28mm, axis (0,0,1), area 668.1mm2, adj f0,f1,f6,f16,f22,f39,f41,f42
  f24: plane 18.2x1.28mm, normal (-1,0,0), area 23.3mm2, adj f1,f2,f9,f15
  f25: plane 12.2x8mm, normal (0,1,0), area 97.6mm2, adj f11,f12,f13,f26
  f26: cylinder r=12.12mm len=12.13mm, axis (0,0,1), area 102.5mm2, adj f11,f12,f18,f25,f27
  f27: plane 18.2x1.28mm, normal (-1,0,0), area 23.3mm2, adj f9,f11,f18,f26
  f28: plane 10x8mm, normal (-1,0,0), area 80mm2, adj f1,f14,f21,f29
  f29: plane 8x6mm, normal (0,-1,0), area 48mm2, adj f1,f10,f14,f28
  f30: plane 8x6mm, normal (0,-1,0), area 48mm2, adj f11,f12,f13,f31
  f31: plane 10x8mm, normal (-1,0,0), area 80mm2, adj f11,f12,f21,f30
  f32: cylinder r=1.82mm len=3.75mm, axis (0,0,1), area 43mm2, adj f16,f36
  f33: plane 5.95x5.95mm, normal (0,0,1), area 17.3mm2, adj f7,f35
  f34: plane 5.95x5.95mm, normal (0,0,1), area 17.3mm2, adj f4,f8
  f35: cylinder r=2.98mm len=24.25mm, axis (0,0,1), area 453.3mm2, adj f6,f33
  f36: plane 5.95x5.95mm, normal (0,0,1), area 17.3mm2, adj f5,f32
  f37: cylinder r=7.7mm len=48.4mm, axis (0,1,0), area 2178.6mm2, adj f4,f5,f9,f21
  f38: cylinder r=3mm len=4mm, axis (0,0,1), area 6.7mm2, adj f1,f2,f42,f43
  f39: plane 12.13x5mm, normal (0,0,1), area 18.9mm2, adj f3,f22,f23,f40,f41
  f40: cylinder r=3mm len=4mm, axis (0,0,1), area 18.8mm2, adj f1,f3,f39,f41
  f41: plane 4x3.79mm, normal (1,0,0), area 15.1mm2, adj f1,f23,f39,f40
  f42: plane 4x3.79mm, normal (-1,0,0), area 15.1mm2, adj f1,f23,f38,f43
  f43: plane 10.72x2.46mm, normal (0,0,1), area 12.4mm2, adj f0,f2,f23,f38,f42
PLACE A t=(10.98,35.66,38.45)mm
PLACE B rot(axis=(0.36,-0.36,-0.86),98.4deg) t=(-47.22,29.66,-4.83)mm
PLACE C rot(axis=(0.36,0.36,0.86),98.4deg) t=(53.19,29.66,-4.83)mm
PLACE D rot(axis=(-1,0,0),90deg) t=(10.98,21.53,30.39)mm
PLACE E t=(2.91,35.58,66.58)mm
MATE fastened D.f0 <-> A.f122  axis (0,1,0) through (-1.14,21.53,30.39)mm
MATE fastened A.f140 <-> E.f5  axis (0,0,1) through (-16.22,54.78,52.58)mm
MATE revolute B.f58 <-> A.f80  axis (0,1,0) through (-26.04,29.66,12.35)mm
MATE revolute C.f52 <-> A.f83  axis (0,1,0) through (32.01,29.66,12.35)mm
